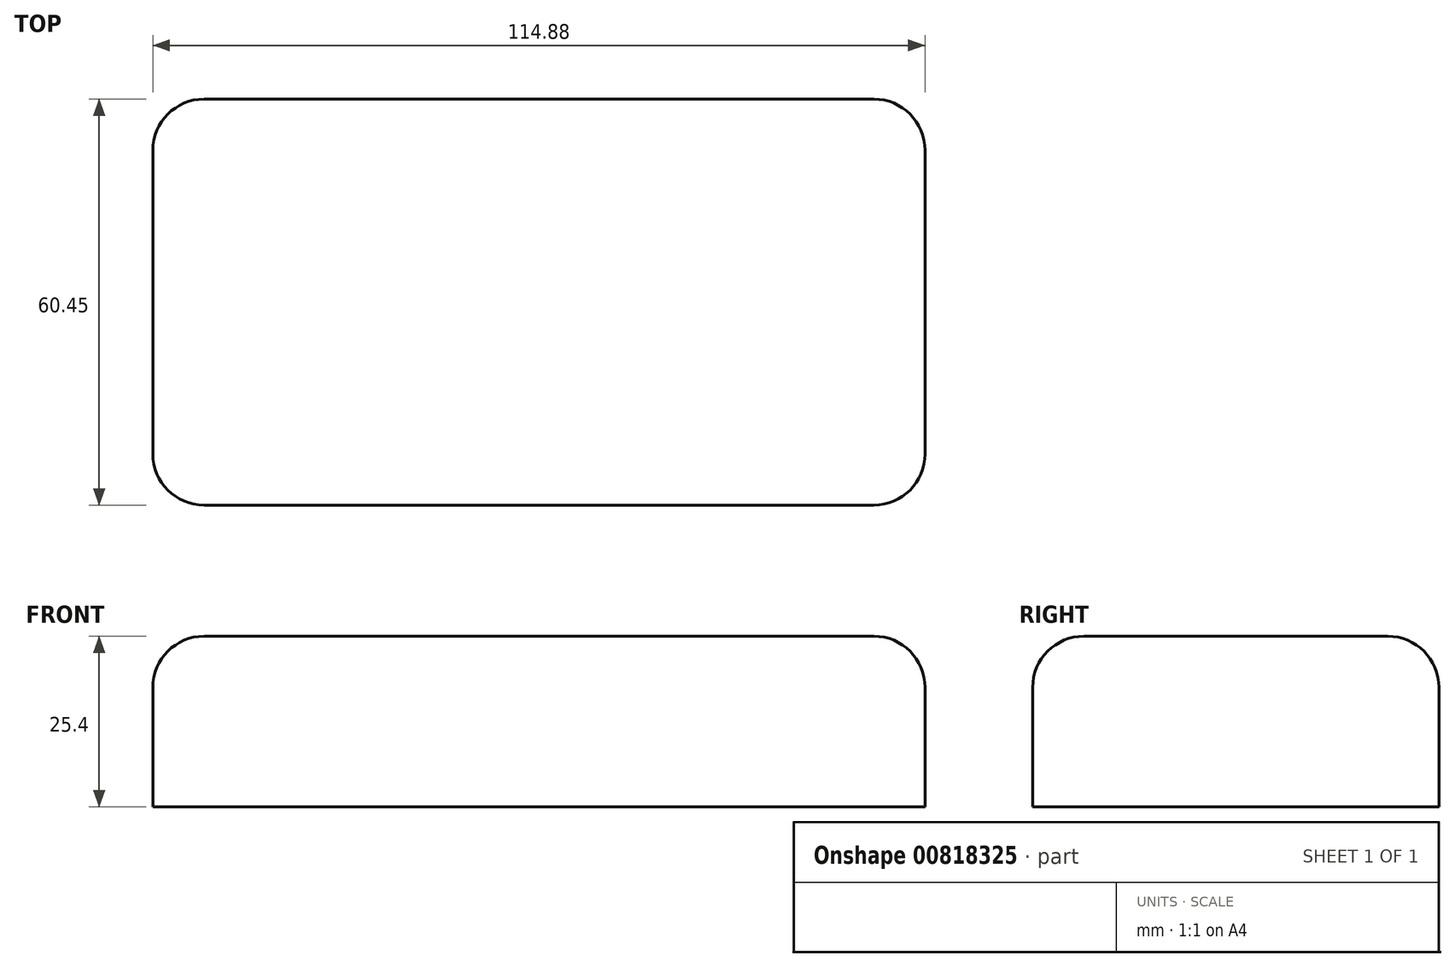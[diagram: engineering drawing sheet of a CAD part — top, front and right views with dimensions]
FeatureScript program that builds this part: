
annotation { "Feature Type Name" : "Feature", "Feature Type Description" : "" }
export const myFeature = defineFeature(function(context is Context, id is Id, definition is map)
    precondition{}
    {
        {
            var Q0;
            Q0=qCreatedBy(makeId("Top.planeOp"),FACE);
            var sketch = newSketch(context, id + "F0", { "sketchPlane" : qUnion([Q0])});
            skLineSegment(sketch, "E0.bottom", {"start": v(-58.94, 25.8) * mm, "end": v(55.94, 25.8) * mm});
            skLineSegment(sketch, "E0.top", {"start": v(-58.94, -34.65) * mm, "end": v(55.94, -34.65) * mm});
            skLineSegment(sketch, "E0.left", {"start": v(-58.94, 25.8) * mm, "end": v(-58.94, -34.65) * mm});
            skLineSegment(sketch, "E0.right", {"start": v(55.94, 25.8) * mm, "end": v(55.94, -34.65) * mm});
            skSolve(sketch);
        }
        {
            var Q0;
            Q0 = qSketchRegion(id + "F0", true);
            extrude(context, id + "F1", {"entities" : qUnion([Q0]), "depth" : 25.4 * mm, "offsetDistance" : 25.4 * mm});
        }
        {
            var Q0;
            Q0=makeQuery(id+"F1.opExtrude","CAP_EDGE",EDGE,{"disambiguationData":[OSD([sQuery(id+"F0.wireOp",EDGE,"E0.top")])],"isStart":false});
            var Q1;
            Q1=makeQuery(id+"F1.opExtrude","CAP_EDGE",EDGE,{"disambiguationData":[OSD([sQuery(id+"F0.wireOp",EDGE,"E0.right")])],"isStart":false});
            var Q2;
            Q2=makeQuery(id+"F1.opExtrude","CAP_EDGE",EDGE,{"disambiguationData":[OSD([sQuery(id+"F0.wireOp",EDGE,"E0.bottom")])],"isStart":false});
            var Q3;
            Q3=makeQuery(id+"F1.opExtrude","CAP_EDGE",EDGE,{"disambiguationData":[OSD([sQuery(id+"F0.wireOp",EDGE,"E0.left")])],"isStart":false});
            var Q4;
            Q4=makeQuery(id+"F1.opExtrude","SWEPT_EDGE",EDGE,{"disambiguationData":[OSD([sQuery(id+"F0.wireOp",EDGE,"E0.top"),sQuery(id+"F0.wireOp",EDGE,"E0.left")])]});
            var Q5;
            Q5=makeQuery(id+"F1.opExtrude","SWEPT_EDGE",EDGE,{"disambiguationData":[OSD([sQuery(id+"F0.wireOp",EDGE,"E0.top"),sQuery(id+"F0.wireOp",EDGE,"E0.right")])]});
            var Q6;
            Q6=makeQuery(id+"F1.opExtrude","SWEPT_EDGE",EDGE,{"disambiguationData":[OSD([sQuery(id+"F0.wireOp",EDGE,"E0.bottom"),sQuery(id+"F0.wireOp",EDGE,"E0.left")])]});
            var Q7;
            Q7=makeQuery(id+"F1.opExtrude","SWEPT_EDGE",EDGE,{"disambiguationData":[OSD([sQuery(id+"F0.wireOp",EDGE,"E0.bottom"),sQuery(id+"F0.wireOp",EDGE,"E0.right")])]});
            fillet(context, id + "F2", {"entities" : qUnion([Q0, Q1, Q2, Q3, Q4, Q5, Q6, Q7]), "radius" : 7.62 * mm, "tangentPropagation" : true, "allowEdgeOverflow" : false});
        }
        {
            var Q0;
            Q0=makeQuery(id+"F1.opExtrude","CAP_FACE",FACE,{"disambiguationData":[OSD([sQuery(id+"F0.wireOp",EDGE,"E0.bottom"),sQuery(id+"F0.wireOp",EDGE,"E0.top"),sQuery(id+"F0.wireOp",EDGE,"E0.left"),sQuery(id+"F0.wireOp",EDGE,"E0.right")])],"isStart":true});
            var sketch = newSketch(context, id + "F3", { "sketchPlane" : qUnion([Q0])});
            skSolve(sketch);
        }
    });
